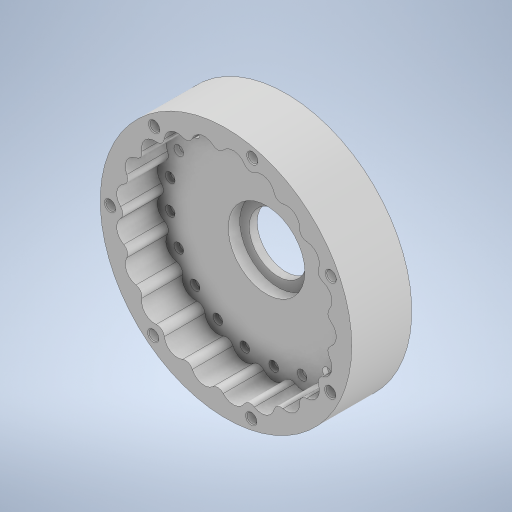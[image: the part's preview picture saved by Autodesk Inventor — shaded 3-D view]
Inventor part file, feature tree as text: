
AUTODESK INVENTOR PART (.ipt)
format: ipt  version: 2023 (Build 270158000, 158)  size: 440,320 bytes
history: native  units: in
note: dims shown in document units (in); Inventor stores cm internally (conversion verified against a paired STEP export)
features: sketch x5, extrude x3, hole x2, pattern_circular x2, reference x2, other x2
ambient origin geometry x8: Origin, YZ Plane, XZ Plane, XY Plane, X Axis, Y Axis, Z Axis, Center Point
bodies: Solid1 (feature_tree)
feature tree (16):
  extrude  "Extrusion1"  Depth=0.0591in
  extrude  "Extrusion2"  Depth=2.6772in TaperAngle=360.0deg
  hole  "Hole1"  [1 undecoded]
  extrude  "Extrusion4"  Depth=0.2362in
  pattern_circular  "Circular Pattern1"  Count=21 Angle=360.0deg
  hole  "Hole2"  [1 undecoded]
  pattern_circular  "Circular Pattern2"  [2 undecoded]
  sketch  "Sketch2"  dims[d0=6.1024in d3=0.0591in]
  reference  "Reference1"
  reference  "Reference2"
  sketch  "Sketch3"  dims[d4=2.6772in d5=8.2677in d7=360.0deg]
  sketch  "Sketch5"  dims[d9=0.9843in d10=0.0in d11=0.4724in d12=0.0in]
  sketch  "Sketch6"  dims[d16=1.4in d17=0.2362in d18=1.86in d19=0.28in d20=90.0deg d21=0.315in d22=0.8108in d23=0.2362in]
  sketch  "Sketch7"  dims[d24=0.1181in d25=0.0in d26=8.2677in d27=360.0deg d29=0.2362in d30=0.2362in d31=0.2756in d32=0.3937in d33=90.0deg d34=0.2362in d35=0.0in d36=2.7559in d37=360.0deg d39=5.6299in]
  other  "Assembly1"
  other  "Bearings:1"
note: 4 required parameter values undecoded (feature->parameter linkage not recoverable at this tier; creation-order binding heuristic only, values carry confidence <= 0.55)
